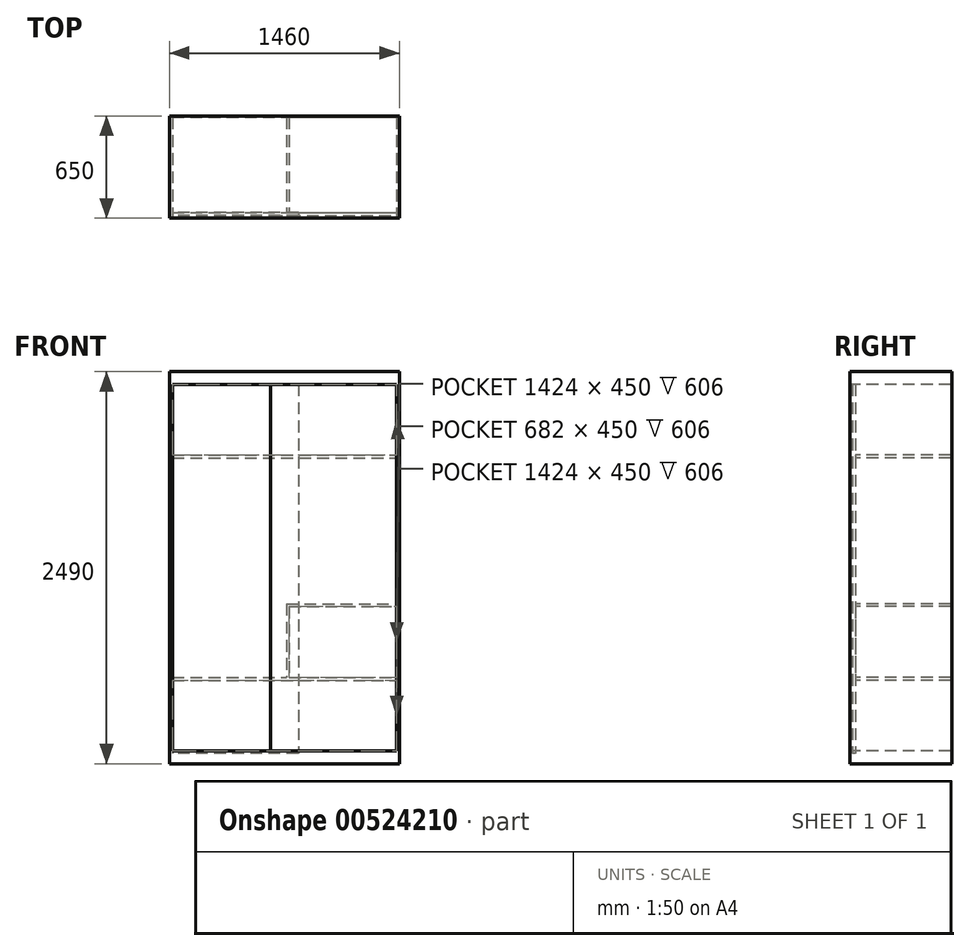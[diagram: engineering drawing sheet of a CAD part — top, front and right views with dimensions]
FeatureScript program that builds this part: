
annotation { "Feature Type Name" : "Feature", "Feature Type Description" : "" }
export const myFeature = defineFeature(function(context is Context, id is Id, definition is map)
    precondition{}
    {
        {
            var Q0;
            Q0=qCreatedBy(makeId("Top.planeOp"),FACE);
            var sketch = newSketch(context, id + "F0", { "sketchPlane" : qUnion([Q0])});
            skLineSegment(sketch, "E0.bottom", {"start": v(0, 0) * mm, "end": v(-1460, 0) * mm});
            skLineSegment(sketch, "E0.top", {"start": v(0, 650) * mm, "end": v(-1460, 650) * mm});
            skLineSegment(sketch, "E0.left", {"start": v(0, 0) * mm, "end": v(0, 650) * mm});
            skLineSegment(sketch, "E0.right", {"start": v(-1460, 0) * mm, "end": v(-1460, 650) * mm});
            skPoint(sketch, "E1.oppositeSnap0", {"position": v(-1460, 325) * mm});
            skLineSegment(sketch, "E1.bottom", {"start": v(-1460, 0) * mm, "end": v(-2355, 0) * mm});
            skLineSegment(sketch, "E1.left", {"start": v(-1460, 0) * mm, "end": v(-1460, 325) * mm});
            skLineSegment(sketch, "E1.right", {"start": v(-2355, 0) * mm, "end": v(-2355, 325) * mm});
            skLineSegment(sketch, "E2.bottom", {"start": v(-1460, 430) * mm, "end": v(-2355, 430) * mm});
            skLineSegment(sketch, "E2.left", {"start": v(-1460, 430) * mm, "end": v(-1460, 325) * mm});
            skLineSegment(sketch, "E2.right", {"start": v(-2355, 430) * mm, "end": v(-2355, 325) * mm});
            skSolve(sketch);
        }
        {
            var Q0;
            {var subQ1=sQuery(id+"F0.wireOp",EDGE,"E0.bottom");Q0=makeQuery(id+"F0.imprint","IMPRINT",FACE,{"disambiguationData":[TD([[makeQuery(id+"F0.imprint","IMPRINT",EDGE,{"derivedFrom":subQ1}),-1.0]])]});}
            extrude(context, id + "F1", {"entities" : qUnion([Q0]), "depth" : 2490 * mm, "offsetDistance" : 25 * mm});
        }
        {
            var Q0;
            Q0=makeQuery(id+"F1.opExtrude","SWEPT_FACE",FACE,{"disambiguationData":[OSD([sQuery(id+"F0.wireOp",EDGE,"E0.bottom")])]});
            var sketch = newSketch(context, id + "F2", { "sketchPlane" : qUnion([Q0])});
            skLineSegment(sketch, "E3.bottom", {"start": v(-1442, 2410) * mm, "end": v(-18, 2410) * mm});
            skLineSegment(sketch, "E3.top", {"start": v(-1442, 80) * mm, "end": v(-18, 80) * mm});
            skLineSegment(sketch, "E3.left", {"start": v(-1442, 2410) * mm, "end": v(-1442, 80) * mm});
            skLineSegment(sketch, "E3.right", {"start": v(-18, 2410) * mm, "end": v(-18, 80) * mm});
            skSolve(sketch);
        }
        {
            var Q0;
            Q0 = qSketchRegion(id + "F2", true);
            extrude(context, id + "F3", {"entities" : qUnion([Q0]), "operationType" : NewBodyOperationType.REMOVE, "oppositeDirection" : true, "depth" : 36 * mm, "offsetDistance" : 25 * mm});
        }
        {
            var Q0;
            Q0=makeQuery(id+"F3.boolean.opBoolean","COPY",FACE,{"derivedFrom":makeQuery(id+"F3.opExtrude","CAP_FACE",FACE,{"disambiguationData":[OSD([sQuery(id+"F2.wireOp",EDGE,"E3.bottom"),sQuery(id+"F2.wireOp",EDGE,"E3.top"),sQuery(id+"F2.wireOp",EDGE,"E3.left"),sQuery(id+"F2.wireOp",EDGE,"E3.right")])],"isStart":false})});
            var sketch = newSketch(context, id + "F4", { "sketchPlane" : qUnion([Q0])});
            skLineSegment(sketch, "E4.bottom", {"start": v(-1442, 2410) * mm, "end": v(-18, 2410) * mm});
            skLineSegment(sketch, "E4.top", {"start": v(-1442, 1960) * mm, "end": v(-18, 1960) * mm});
            skLineSegment(sketch, "E4.left", {"start": v(-1442, 2410) * mm, "end": v(-1442, 1960) * mm});
            skLineSegment(sketch, "E4.right", {"start": v(-18, 2410) * mm, "end": v(-18, 1960) * mm});
            skLineSegment(sketch, "E5.bottom", {"start": v(-1442, 1942) * mm, "end": v(-18, 1942) * mm});
            skLineSegment(sketch, "E5.top", {"start": v(-718, 1016) * mm, "end": v(-18, 1016) * mm});
            skLineSegment(sketch, "E5.right", {"start": v(-18, 1942) * mm, "end": v(-18, 1016) * mm});
            skLineSegment(sketch, "E6.top", {"start": v(-1442, 548) * mm, "end": v(-718, 548) * mm});
            skLineSegment(sketch, "E6.right", {"start": v(-718, 1016) * mm, "end": v(-718, 548) * mm});
            skLineSegment(sketch, "E7.left", {"start": v(-1442, 530) * mm, "end": v(-1442, 104.26) * mm});
            skLineSegment(sketch, "E8.bottom", {"start": v(-700, 998) * mm, "end": v(-18, 998) * mm});
            skLineSegment(sketch, "E8.top", {"start": v(-700, 548) * mm, "end": v(-18, 548) * mm});
            skLineSegment(sketch, "E8.left", {"start": v(-700, 998) * mm, "end": v(-700, 548) * mm});
            skLineSegment(sketch, "E8.right", {"start": v(-18, 998) * mm, "end": v(-18, 548) * mm});
            skLineSegment(sketch, "E9.bottom", {"start": v(-1442, 530) * mm, "end": v(-18, 530) * mm});
            skLineSegment(sketch, "E9.right", {"start": v(-18, 530) * mm, "end": v(-18, 80) * mm});
            skSolve(sketch);
        }
        {
            var Q0;
            Q0=makeQuery(id+"F4.imprint","IMPRINT",FACE,{"disambiguationData":[TD([[makeQuery(id+"F4.imprint","IMPRINT",EDGE,{"derivedFrom":sQuery(id+"F4.wireOp",EDGE,"E4.bottom")}),-1.0]])]});
            var Q1;
            Q1=makeQuery(id+"F4.imprint","IMPRINT",FACE,{"disambiguationData":[TD([[makeQuery(id+"F4.imprint","IMPRINT",EDGE,{"derivedFrom":sQuery(id+"F4.wireOp",EDGE,"E8.bottom")}),-1.0]])]});
            var Q2;
            {var subQ1=sQuery(id+"F4.wireOp",EDGE,"E5.bottom");Q2=makeQuery(id+"F4.imprint","IMPRINT",FACE,{"disambiguationData":[TD([[makeQuery(id+"F4.imprint","IMPRINT",EDGE,{"derivedFrom":subQ1}),-1.0]])]});}
            var Q3;
            Q3=makeQuery(id+"F4.imprint","IMPRINT",FACE,{"disambiguationData":[TD([[makeQuery(id+"F4.imprint","IMPRINT",EDGE,{"derivedFrom":sQuery(id+"F4.wireOp",EDGE,"E9.bottom")}),-1.0]])]});
            extrude(context, id + "F5", {"entities" : qUnion([Q0, Q1, Q2, Q3]), "operationType" : NewBodyOperationType.REMOVE, "oppositeDirection" : true, "depth" : 606 * mm, "offsetDistance" : 25 * mm});
        }
        {
            var Q0;
            Q0=makeQuery(id+"F5.boolean.opBoolean","MERGE",FACE,{"derivedFrom":[makeQuery(id+"F3.boolean.opBoolean","COPY",FACE,{"derivedFrom":makeQuery(id+"F3.opExtrude","SWEPT_FACE",FACE,{"disambiguationData":[OSD([sQuery(id+"F2.wireOp",EDGE,"E3.right")])]})}),makeQuery(id+"F5.opExtrude","SWEPT_FACE",FACE,{"disambiguationData":[OSD([sQuery(id+"F4.wireOp",EDGE,"E4.right")])]}),makeQuery(id+"F5.opExtrude","SWEPT_FACE",FACE,{"disambiguationData":[OSD([sQuery(id+"F4.wireOp",EDGE,"E5.right")])]}),makeQuery(id+"F5.opExtrude","SWEPT_FACE",FACE,{"disambiguationData":[OSD([sQuery(id+"F4.wireOp",EDGE,"E8.right")])]}),makeQuery(id+"F5.opExtrude","SWEPT_FACE",FACE,{"disambiguationData":[OSD([sQuery(id+"F4.wireOp",EDGE,"E9.right")])]})]});
            var sketch = newSketch(context, id + "F6", { "sketchPlane" : qUnion([Q0])});
            skLineSegment(sketch, "E10.0", {"start": v(0, 2410) * mm, "end": v(0, 80) * mm});
            skLineSegment(sketch, "E11.bottom", {"start": v(0, 2410) * mm, "end": v(-18, 2410) * mm});
            skLineSegment(sketch, "E11.top", {"start": v(0, 80) * mm, "end": v(-18, 80) * mm});
            skLineSegment(sketch, "E11.right", {"start": v(-18, 2410) * mm, "end": v(-18, 80) * mm});
            skSolve(sketch);
        }
        {
            var Q0;
            Q0 = qSketchRegion(id + "F6", true);
            extrude(context, id + "F7", {"entities" : qUnion([Q0]), "depth" : 800 * mm, "offsetDistance" : 25 * mm});
        }
        {
            var Q0;
            {var subQ0=sQuery(id+"F2.wireOp",EDGE,"E3.left");Q0=makeQuery(id+"F5.boolean.opBoolean","MERGE",FACE,{"derivedFrom":[makeQuery(id+"F3.boolean.opBoolean","COPY",FACE,{"derivedFrom":makeQuery(id+"F3.opExtrude","SWEPT_FACE",FACE,{"disambiguationData":[OSD([subQ0])]})}),makeQuery(id+"F5.opExtrude","SWEPT_FACE",FACE,{"disambiguationData":[OSD([sQuery(id+"F4.wireOp",EDGE,"E4.left")])]}),makeQuery(id+"F5.opExtrude","SWEPT_FACE",FACE,{"disambiguationData":[OSD([subQ0,sQuery(id+"F4.wireOp",EDGE,"E7.left")])]}),makeQuery(id+"F5.opExtrude","SWEPT_FACE",FACE,{"disambiguationData":[OSD([subQ0])]})]});}
            var sketch = newSketch(context, id + "F8", { "sketchPlane" : qUnion([Q0])});
            skLineSegment(sketch, "E12.bottom", {"start": v(36, 2410) * mm, "end": v(18, 2410) * mm});
            skLineSegment(sketch, "E12.top", {"start": v(36, 65.12) * mm, "end": v(18, 65.12) * mm});
            skLineSegment(sketch, "E12.left", {"start": v(36, 2410) * mm, "end": v(36, 65.12) * mm});
            skLineSegment(sketch, "E12.right", {"start": v(18, 2410) * mm, "end": v(18, 65.12) * mm});
            skSolve(sketch);
        }
        {
            var Q0;
            Q0 = qSketchRegion(id + "F8", true);
            extrude(context, id + "F9", {"entities" : qUnion([Q0]), "depth" : 800 * mm, "offsetDistance" : 25 * mm});
        }
    });
